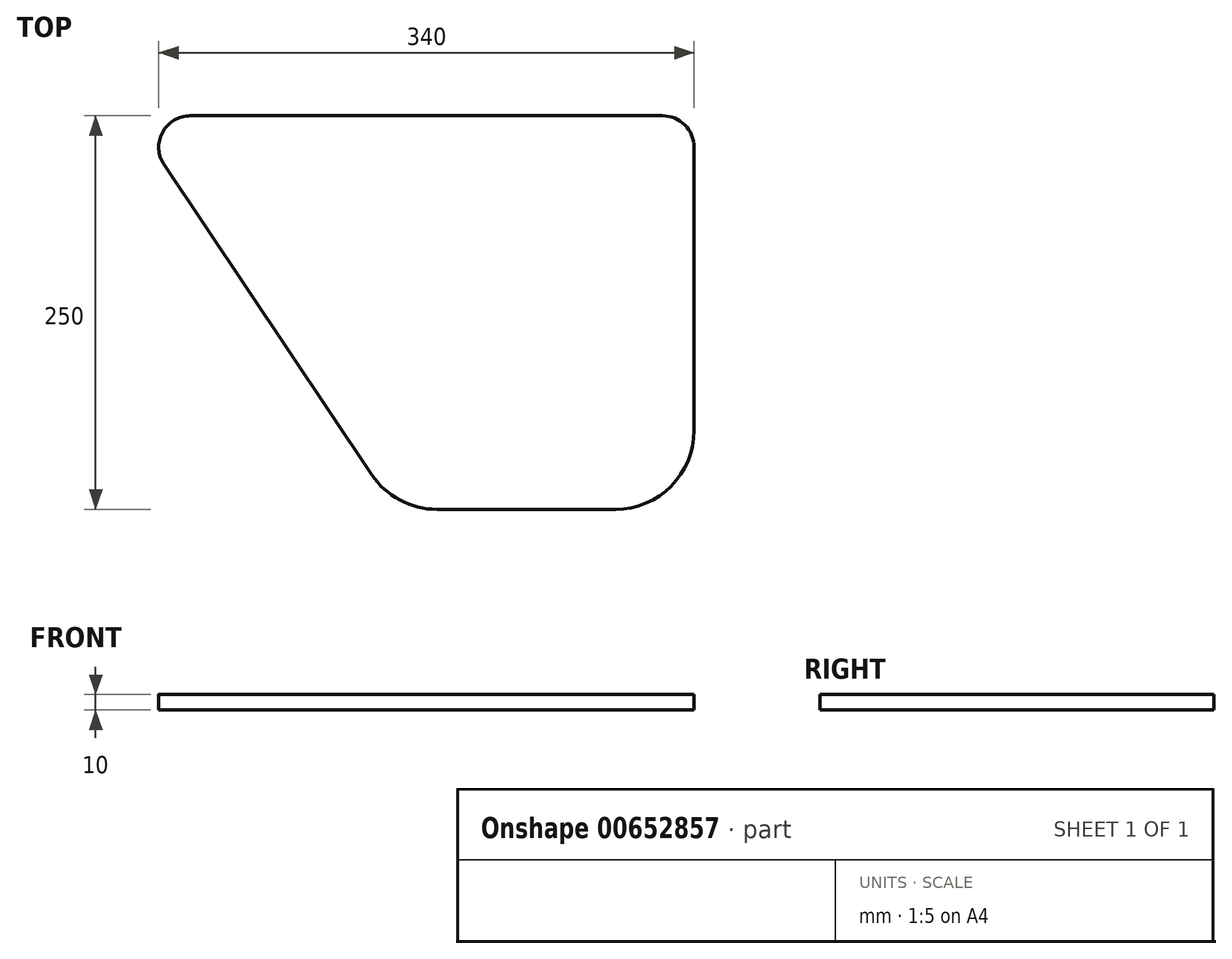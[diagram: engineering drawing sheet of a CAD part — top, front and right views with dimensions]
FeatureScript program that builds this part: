
annotation { "Feature Type Name" : "Feature", "Feature Type Description" : "" }
export const myFeature = defineFeature(function(context is Context, id is Id, definition is map)
    precondition{}
    {
        {
            var Q0;
            Q0=qCreatedBy(makeId("Top.planeOp"),FACE);
            var sketch = newSketch(context, id + "F0", { "sketchPlane" : qUnion([Q0])});
            skLineSegment(sketch, "E0", {"start": v(0, 50) * mm, "end": v(0, 230) * mm});
            skLineSegment(sketch, "E1", {"start": v(-20, 250) * mm, "end": v(-320, 250) * mm});
            skLineSegment(sketch, "E2", {"start": v(-336.62, 218.87) * mm, "end": v(-204.85, 22.17) * mm});
            skLineSegment(sketch, "E3", {"start": v(-163.31, 0) * mm, "end": v(-50, 0) * mm});
            skArc(sketch, "E4", {"start": v(-320, 250) * mm, "mid": v(-337.64, 239.42) * mm, "end": v(-336.62, 218.87) * mm});
            skPoint(sketch, "E5.visualSharp", {"position": v(0, 250) * mm});
            skArc(sketch, "E5.filletArc", {"start": v(0, 230) * mm, "mid": v(-5.86, 244.14) * mm, "end": v(-20, 250) * mm});
            skPoint(sketch, "E6.visualSharp", {"position": v(0, 0) * mm});
            skArc(sketch, "E6.filletArc", {"start": v(-50, 0) * mm, "mid": v(-14.64, 14.64) * mm, "end": v(0, 50) * mm});
            skPoint(sketch, "E7.visualSharp", {"position": v(-190, 0) * mm});
            skArc(sketch, "E7.filletArc", {"start": v(-204.85, 22.17) * mm, "mid": v(-186.86, 5.9) * mm, "end": v(-163.31, 0) * mm});
            skSolve(sketch);
        }
        {
            var Q0;
            Q0=makeQuery(id+"F0.imprint","IMPRINT",FACE,{"disambiguationData":[TD([[makeQuery(id+"F0.imprint","IMPRINT",EDGE,{"derivedFrom":sQuery(id+"F0.wireOp",EDGE,"E0")}),1.0]])]});
            extrude(context, id + "F1", {"entities" : qUnion([Q0]), "depth" : 10 * mm, "offsetDistance" : 25 * mm});
        }
    });
